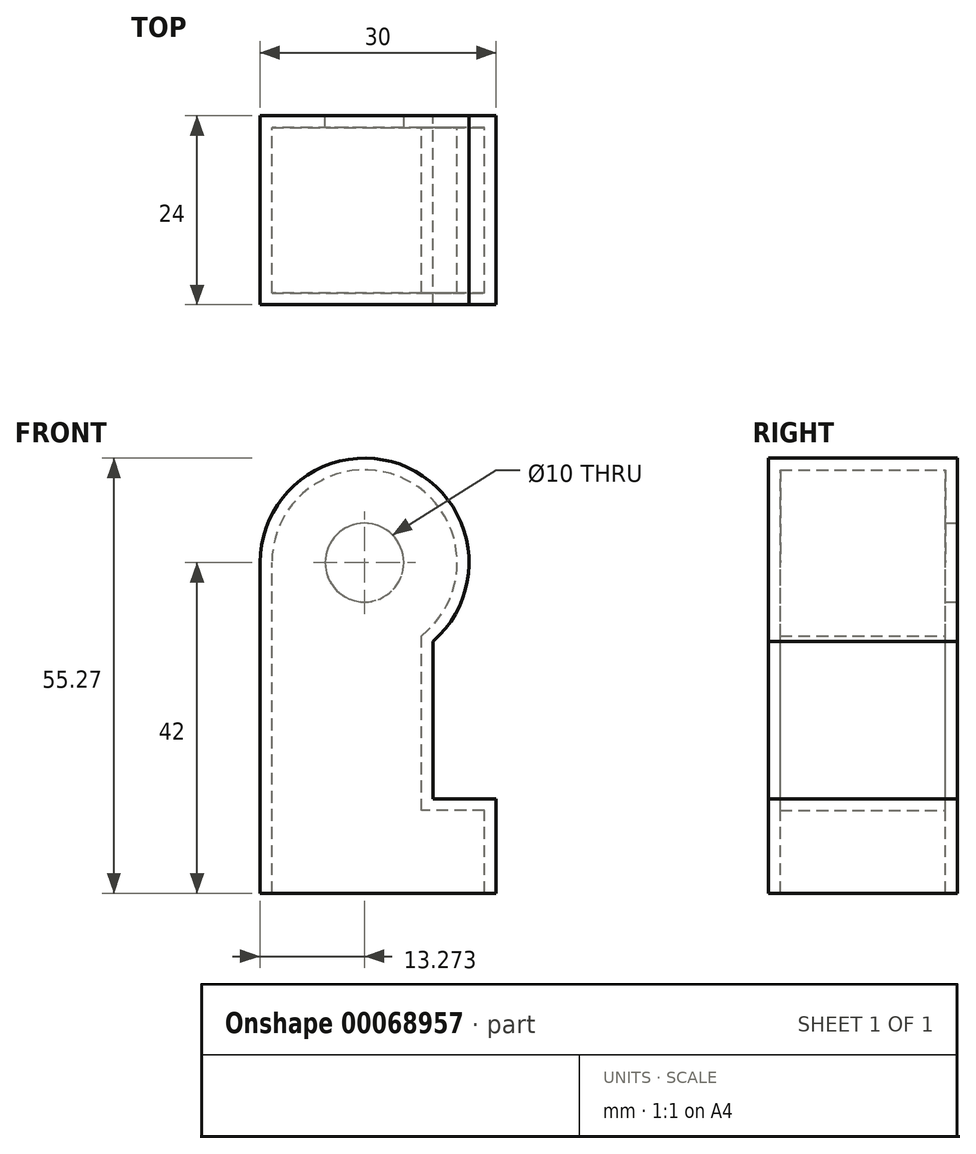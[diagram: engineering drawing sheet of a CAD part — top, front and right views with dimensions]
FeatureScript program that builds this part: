
annotation { "Feature Type Name" : "Feature", "Feature Type Description" : "" }
export const myFeature = defineFeature(function(context is Context, id is Id, definition is map)
    precondition{}
    {
        {
            var Q0;
            Q0=qCreatedBy(makeId("Front.planeOp"),FACE);
            var sketch = newSketch(context, id + "F0", { "sketchPlane" : qUnion([Q0])});
            skLineSegment(sketch, "E0", {"start": v(0, 0) * mm, "end": v(0, 42) * mm});
            skLineSegment(sketch, "E1", {"start": v(0, 0) * mm, "end": v(30, 0) * mm});
            skLineSegment(sketch, "E2", {"start": v(30, 0) * mm, "end": v(30, 12) * mm});
            skLineSegment(sketch, "E3", {"start": v(30, 12) * mm, "end": v(22, 12) * mm});
            skLineSegment(sketch, "E4", {"start": v(22, 12) * mm, "end": v(22, 32) * mm});
            skArc(sketch, "E5", {"start": v(22, 32) * mm, "mid": v(18.77, 54.08) * mm, "end": v(0, 42) * mm});
            skSolve(sketch);
        }
        {
            var Q0;
            Q0=makeQuery(id+"F0.imprint","IMPRINT",FACE,{"disambiguationData":[TD([[makeQuery(id+"F0.imprint","IMPRINT",EDGE,{"derivedFrom":sQuery(id+"F0.wireOp",EDGE,"E0")}),-1.0]])]});
            extrude(context, id + "F1", {"entities" : qUnion([Q0]), "depth" : 24 * mm});
        }
        {
            var Q0;
            Q0=makeQuery(id+"F1.opExtrude","SWEPT_FACE",FACE,{"disambiguationData":[OSD([sQuery(id+"F0.wireOp",EDGE,"E1")])]});
            shell(context, id + "F2", {"entities" : qUnion([Q0]), "thickness" : 1.5 * mm});
        }
        {
            var Q0;
            Q0=makeQuery(id+"F1.opExtrude","CAP_FACE",FACE,{"disambiguationData":[OSD([sQuery(id+"F0.wireOp",EDGE,"E0"),sQuery(id+"F0.wireOp",EDGE,"E1"),sQuery(id+"F0.wireOp",EDGE,"E2"),sQuery(id+"F0.wireOp",EDGE,"E3"),sQuery(id+"F0.wireOp",EDGE,"E4"),sQuery(id+"F0.wireOp",EDGE,"E5")])],"isStart":true});
            var sketch = newSketch(context, id + "F3", { "sketchPlane" : qUnion([Q0])});
            skCircle(sketch, "E6", {"center": v(-13.27, 42) * mm, "radius": 5 * mm});
            skSolve(sketch);
        }
        {
            var Q0;
            Q0=makeQuery(id+"F3.imprint","IMPRINT",FACE,{"disambiguationData":[TD([[makeQuery(id+"F3.imprint","IMPRINT",EDGE,{"derivedFrom":sQuery(id+"F3.wireOp",EDGE,"E6")}),1.0]])]});
            extrude(context, id + "F4", {"entities" : qUnion([Q0]), "operationType" : NewBodyOperationType.REMOVE, "oppositeDirection" : true, "depth" : 5 * mm});
        }
    });
